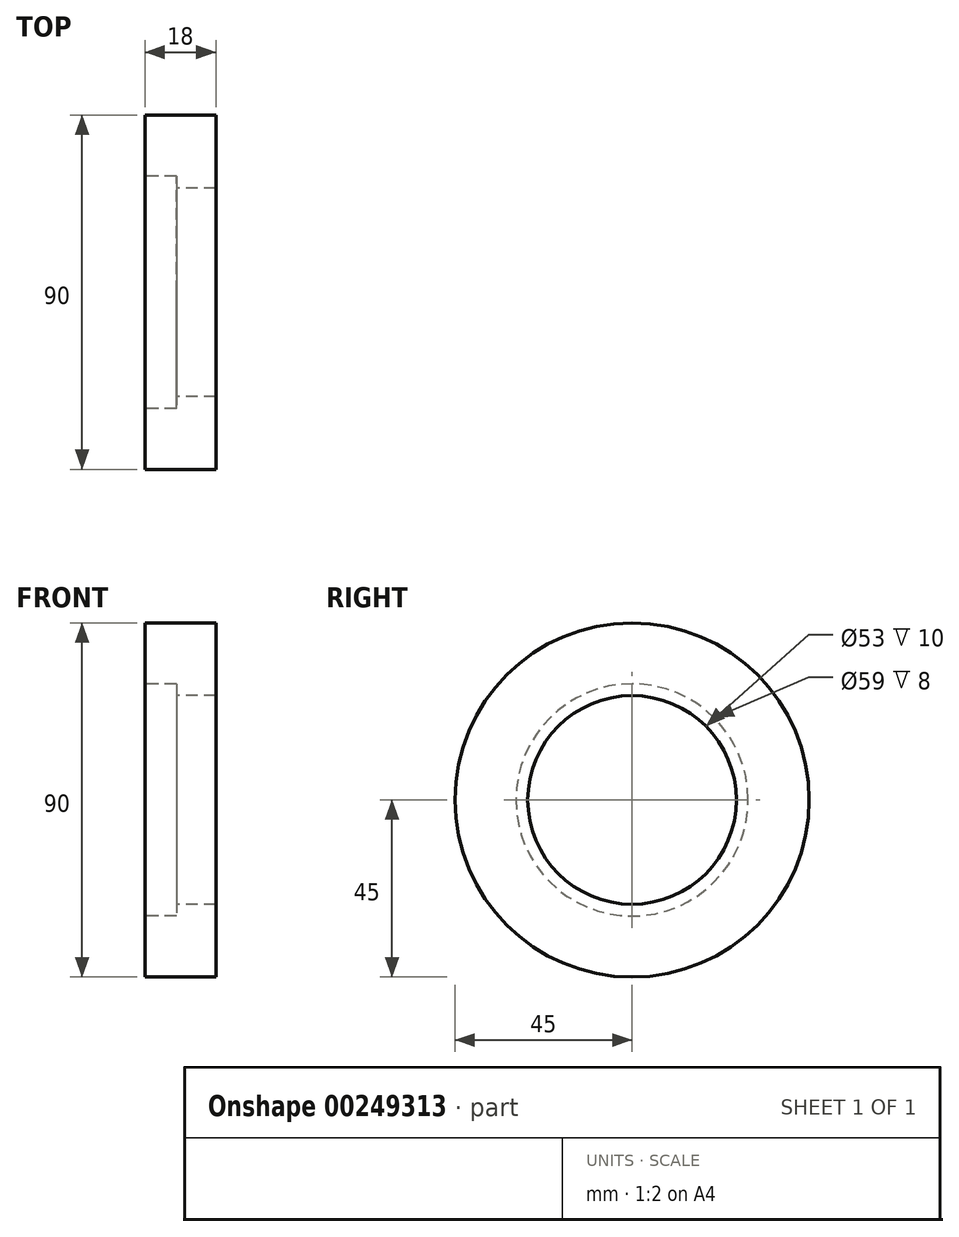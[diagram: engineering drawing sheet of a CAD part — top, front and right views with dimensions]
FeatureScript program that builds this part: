
annotation { "Feature Type Name" : "Feature", "Feature Type Description" : "" }
export const myFeature = defineFeature(function(context is Context, id is Id, definition is map)
    precondition{}
    {
        {
            var Q0;
            Q0=qCreatedBy(makeId("Front.planeOp"),FACE);
            var sketch = newSketch(context, id + "F0", { "sketchPlane" : qUnion([Q0])});
            skLineSegment(sketch, "E0", {"start": v(0, 26.5) * mm, "end": v(0, 45) * mm});
            skLineSegment(sketch, "E1", {"start": v(0, 45) * mm, "end": v(-18, 45) * mm});
            skLineSegment(sketch, "E2", {"start": v(-10, 26.5) * mm, "end": v(-10, 29.5) * mm});
            skLineSegment(sketch, "E3", {"start": v(-10, 29.5) * mm, "end": v(-18, 29.5) * mm});
            skLineSegment(sketch, "E4", {"start": v(0, 0) * mm, "end": v(24.78, 0) * mm});
            skLineSegment(sketch, "E5", {"start": v(-10, 26.5) * mm, "end": v(0, 26.5) * mm});
            skLineSegment(sketch, "E6", {"start": v(-18, 29.5) * mm, "end": v(-18, 45) * mm});
            skSolve(sketch);
        }
        {
            var Q0;
            Q0=makeQuery(id+"F0.imprint","IMPRINT",FACE,{"disambiguationData":[TD([[makeQuery(id+"F0.imprint","IMPRINT",EDGE,{"derivedFrom":sQuery(id+"F0.wireOp",EDGE,"E0")}),1.0]])]});
            var Q1;
            Q1=sQuery(id+"F0.wireOp",EDGE,"E4");
            revolve(context, id + "F1", {"entities" : qUnion([Q0]), "axis" : qUnion([Q1]), "revolveType" : RevolveType.FULL});
        }
    });
